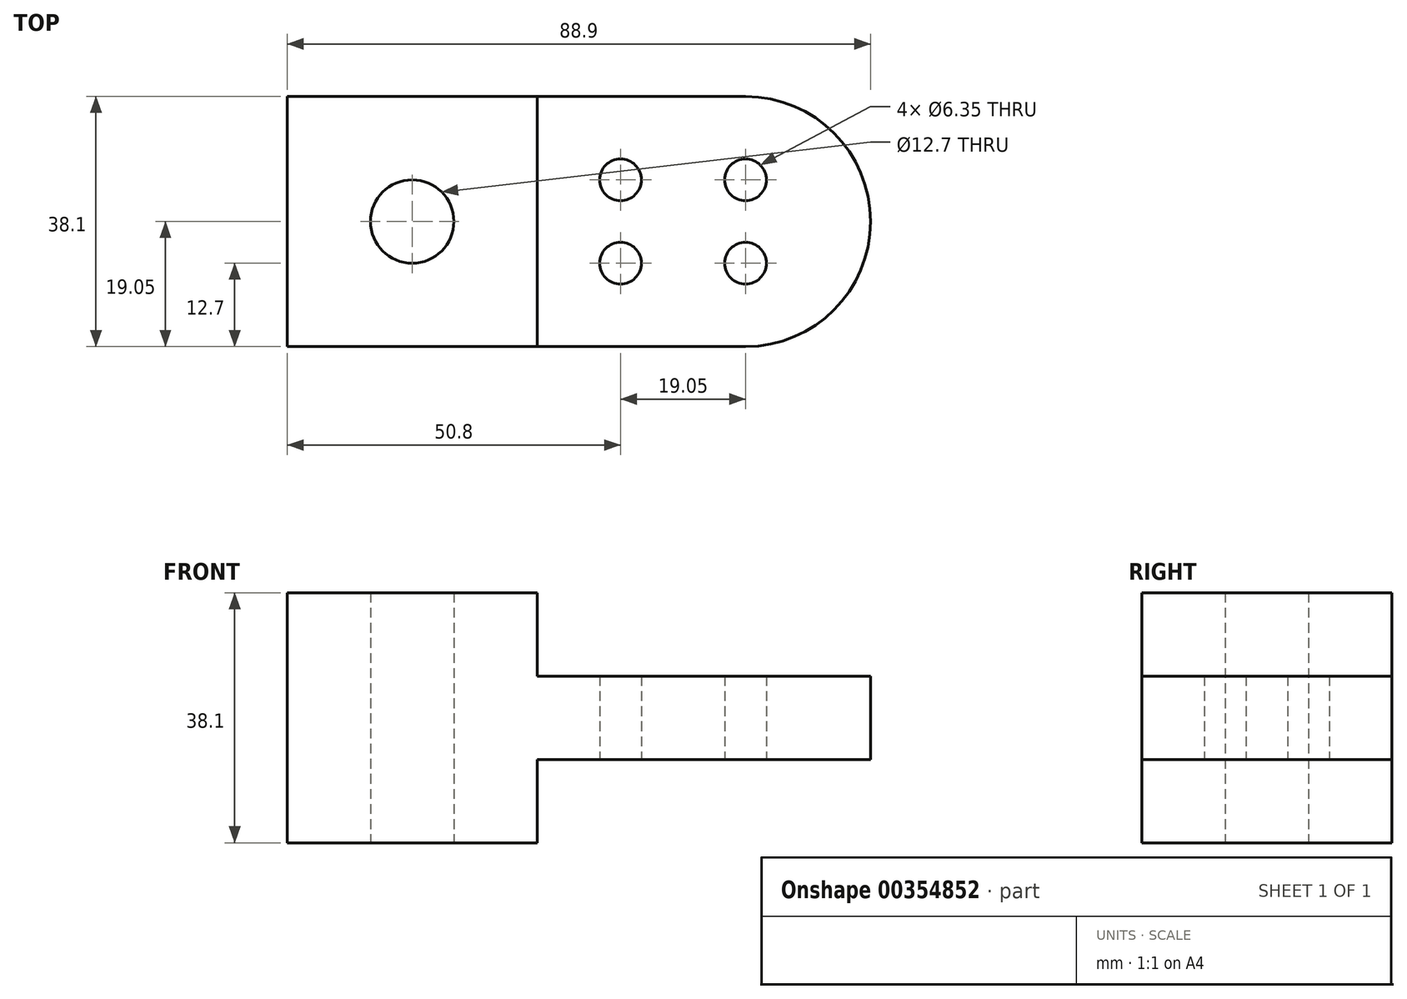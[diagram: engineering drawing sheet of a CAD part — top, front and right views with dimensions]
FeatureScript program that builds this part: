
annotation { "Feature Type Name" : "Feature", "Feature Type Description" : "" }
export const myFeature = defineFeature(function(context is Context, id is Id, definition is map)
    precondition{}
    {
        {
            var Q0;
            Q0=qCreatedBy(makeId("Top.planeOp"),FACE);
            var sketch = newSketch(context, id + "F0", { "sketchPlane" : qUnion([Q0])});
            skLineSegment(sketch, "E0.bottom", {"start": v(0, 0) * mm, "end": v(38.1, 0) * mm});
            skLineSegment(sketch, "E0.top", {"start": v(0, 38.1) * mm, "end": v(38.1, 38.1) * mm});
            skLineSegment(sketch, "E0.left", {"start": v(0, 0) * mm, "end": v(0, 38.1) * mm});
            skLineSegment(sketch, "E0.right", {"start": v(38.1, 0) * mm, "end": v(38.1, 38.1) * mm});
            skLineSegment(sketch, "E1", {"start": v(38.1, 38.1) * mm, "end": v(69.85, 38.1) * mm});
            skLineSegment(sketch, "E2", {"start": v(38.1, 0) * mm, "end": v(69.85, 0) * mm});
            skArc(sketch, "E3", {"start": v(69.85, 0) * mm, "mid": v(88.9, 19.05) * mm, "end": v(69.85, 38.1) * mm});
            skCircle(sketch, "E4", {"center": v(19.05, 19.05) * mm, "radius": 6.35 * mm});
            skPoint(sketch, "E4.centerSnap0", {"position": v(0, 19.05) * mm});
            skPoint(sketch, "E4.centerSnap1", {"position": v(19.05, 38.1) * mm});
            skCircle(sketch, "E5", {"center": v(50.8, 25.4) * mm, "radius": 3.18 * mm});
            skCircle(sketch, "E6", {"center": v(69.85, 25.4) * mm, "radius": 3.18 * mm});
            skCircle(sketch, "E7", {"center": v(50.8, 12.7) * mm, "radius": 3.18 * mm});
            skCircle(sketch, "E8", {"center": v(69.85, 12.7) * mm, "radius": 3.18 * mm});
            skLineSegment(sketch, "E9", {"start": v(-34, 25.4) * mm, "end": v(116.32, 25.4) * mm, "construction": true});
            skLineSegment(sketch, "E10", {"start": v(50.8, 51.19) * mm, "end": v(50.8, -26.22) * mm, "construction": true});
            skLineSegment(sketch, "E11", {"start": v(-34.56, 12.7) * mm, "end": v(117.32, 12.7) * mm, "construction": true});
            skLineSegment(sketch, "E12", {"start": v(69.85, 50.35) * mm, "end": v(69.85, -23.25) * mm, "construction": true});
            skSolve(sketch);
        }
        {
            var Q0;
            Q0=makeQuery(id+"F0.imprint","IMPRINT",FACE,{"disambiguationData":[TD([[makeQuery(id+"F0.imprint","IMPRINT",EDGE,{"derivedFrom":sQuery(id+"F0.wireOp",EDGE,"E0.bottom")}),1.0]])]});
            extrude(context, id + "F1", {"entities" : qUnion([Q0]), "depth" : 38.1 * mm, "symmetric" : true});
        }
        {
            var Q0;
            Q0=makeQuery(id+"F0.imprint","IMPRINT",FACE,{"disambiguationData":[TD([[makeQuery(id+"F0.imprint","IMPRINT",EDGE,{"derivedFrom":sQuery(id+"F0.wireOp",EDGE,"E0.right")}),-1.0]])]});
            extrude(context, id + "F2", {"entities" : qUnion([Q0]), "operationType" : NewBodyOperationType.ADD, "depth" : 12.7 * mm, "symmetric" : true});
        }
    });
